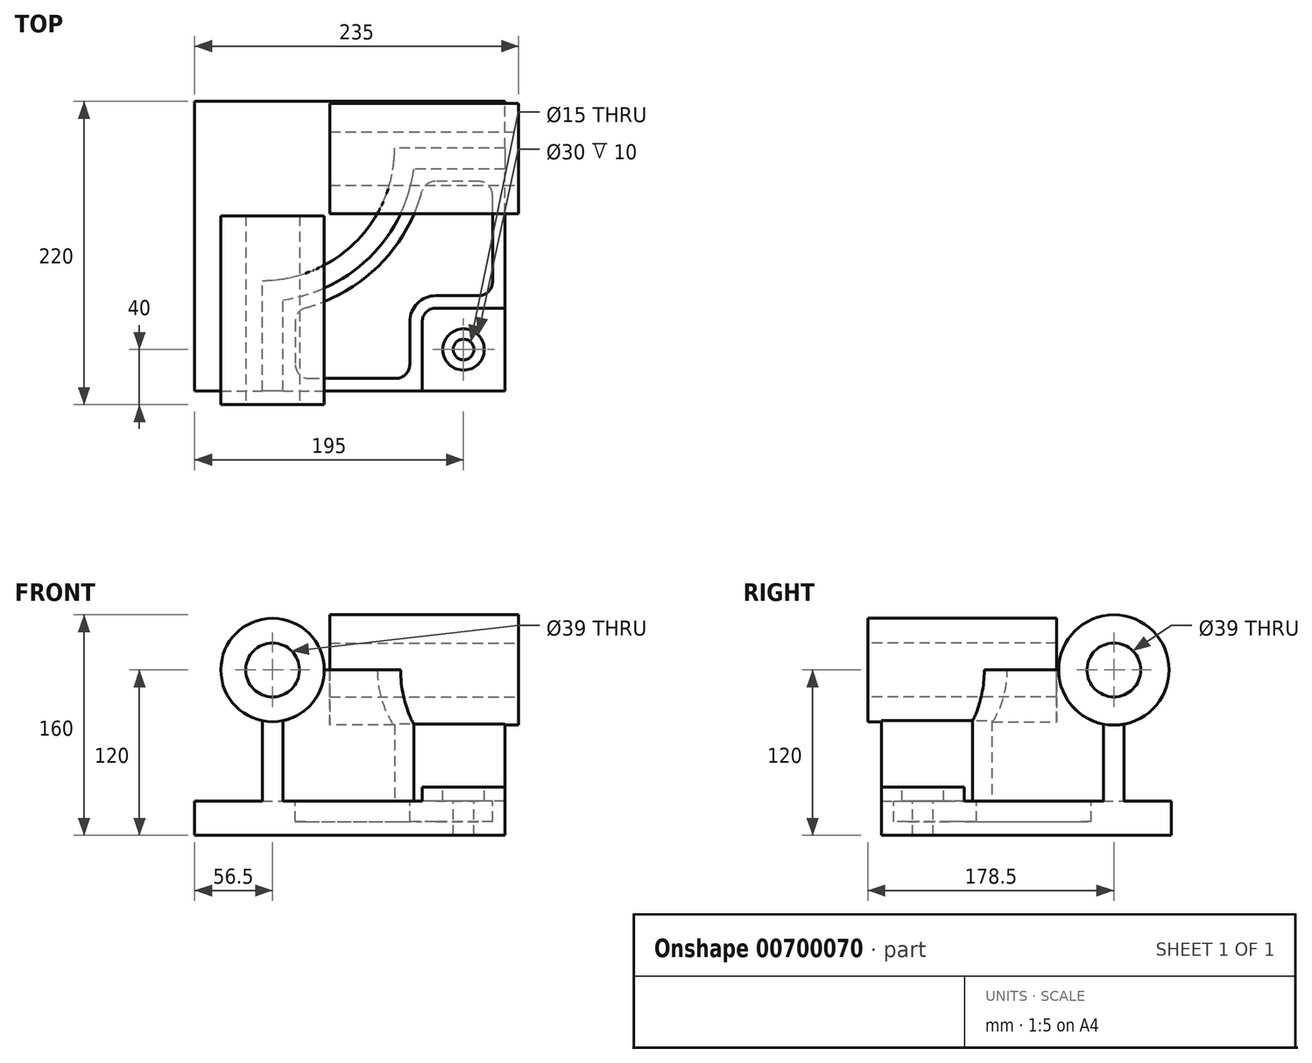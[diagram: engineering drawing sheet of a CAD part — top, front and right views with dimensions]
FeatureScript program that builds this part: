
annotation { "Feature Type Name" : "Feature", "Feature Type Description" : "" }
export const myFeature = defineFeature(function(context is Context, id is Id, definition is map)
    precondition{}
    {
        {
            var Q0;
            Q0=qCreatedBy(makeId("Top.planeOp"),FACE);
            var sketch = newSketch(context, id + "F0", { "sketchPlane" : qUnion([Q0])});
            skLineSegment(sketch, "E0.bottom", {"start": v(-112.5, -105) * mm, "end": v(112.5, -105) * mm});
            skLineSegment(sketch, "E0.top", {"start": v(-112.5, 105) * mm, "end": v(112.5, 105) * mm});
            skLineSegment(sketch, "E0.left", {"start": v(-112.5, -105) * mm, "end": v(-112.5, 105) * mm});
            skLineSegment(sketch, "E0.right", {"start": v(112.5, -105) * mm, "end": v(112.5, 105) * mm});
            skPoint(sketch, "E0.middle", {"position": v(0, 0) * mm});
            skSolve(sketch);
        }
        {
            var Q0;
            Q0=makeQuery(id+"F0.imprint","IMPRINT",FACE,{"disambiguationData":[TD([[makeQuery(id+"F0.imprint","IMPRINT",EDGE,{"derivedFrom":sQuery(id+"F0.wireOp",EDGE,"E0.bottom")}),1.0]])]});
            extrude(context, id + "F1", {"entities" : qUnion([Q0]), "depth" : 25 * mm, "offsetDistance" : 25 * mm});
        }
        {
            var Q0;
            Q0=makeQuery(id+"F1.opExtrude","CAP_FACE",FACE,{"disambiguationData":[OSD([sQuery(id+"F0.wireOp",EDGE,"E0.bottom"),sQuery(id+"F0.wireOp",EDGE,"E0.top"),sQuery(id+"F0.wireOp",EDGE,"E0.left"),sQuery(id+"F0.wireOp",EDGE,"E0.right")])],"isStart":false});
            var sketch = newSketch(context, id + "F2", { "sketchPlane" : qUnion([Q0])});
            skLineSegment(sketch, "E1", {"start": v(-90.07, -105) * mm, "end": v(-63.5, -105) * mm});
            skLineSegment(sketch, "E2", {"start": v(-63.5, -105) * mm, "end": v(-63.5, -25) * mm});
            skLineSegment(sketch, "E3", {"start": v(112.5, 71) * mm, "end": v(32.5, 71) * mm});
            skArc(sketch, "E4", {"start": v(-63.5, -25) * mm, "mid": v(4.38, 3.12) * mm, "end": v(32.5, 71) * mm});
            skLineSegment(sketch, "E5", {"start": v(-63.5, 71) * mm, "end": v(-63.5, -25) * mm, "construction": true});
            skLineSegment(sketch, "E6", {"start": v(-63.5, 71) * mm, "end": v(32.5, 71) * mm, "construction": true});
            skLineSegment(sketch, "E7.0", {"start": v(112.5, 56) * mm, "end": v(46.48, 56) * mm});
            skArc(sketch, "E7.1", {"start": v(-48.5, -38.98) * mm, "mid": v(14.99, -7.49) * mm, "end": v(46.48, 56) * mm});
            skLineSegment(sketch, "E7.2", {"start": v(-48.5, -105) * mm, "end": v(-48.5, -38.98) * mm});
            skLineSegment(sketch, "E8.0", {"start": v(112.5, -105) * mm, "end": v(112.5, 105) * mm});
            skLineSegment(sketch, "E9.0", {"start": v(-112.5, -105) * mm, "end": v(112.5, -105) * mm});
            skSolve(sketch);
        }
        {
            var Q0;
            {var subQ2=sQuery(id+"F2.wireOp",EDGE,"E2");Q0=makeQuery(id+"F2.imprint","IMPRINT",FACE,{"disambiguationData":[TD([[makeQuery(id+"F2.imprint","IMPRINT",EDGE,{"derivedFrom":subQ2}),-1.0]])]});}
            extrude(context, id + "F3", {"entities" : qUnion([Q0]), "operationType" : NewBodyOperationType.ADD, "depth" : 95 * mm, "offsetDistance" : 25 * mm});
        }
        {
            var Q0;
            Q0=makeQuery(id+"F3.boolean.opBoolean","MERGE",FACE,{"derivedFrom":[makeQuery(id+"F1.opExtrude","SWEPT_FACE",FACE,{"disambiguationData":[OSD([sQuery(id+"F0.wireOp",EDGE,"E0.bottom")])]}),makeQuery(id+"F3.opExtrude","SWEPT_FACE",FACE,{"disambiguationData":[OSD([sQuery(id+"F2.wireOp",EDGE,"E9.0")])]})]});
            var sketch = newSketch(context, id + "F4", { "sketchPlane" : qUnion([Q0])});
            skCircle(sketch, "E10", {"center": v(-56, 120) * mm, "radius": 37.5 * mm});
            skSolve(sketch);
        }
        {
            var Q0;
            Q0 = qSketchRegion(id + "F4", true);
            extrude(context, id + "F5", {"entities" : qUnion([Q0]), "operationType" : NewBodyOperationType.ADD, "depth" : 10 * mm, "offsetDistance" : 25 * mm, "hasSecondDirection" : true, "secondDirectionOppositeDirection" : true, "secondDirectionDepth" : 127 * mm});
        }
        {
            var Q0;
            Q0=makeQuery(id+"F3.boolean.opBoolean","MERGE",FACE,{"derivedFrom":[makeQuery(id+"F1.opExtrude","SWEPT_FACE",FACE,{"disambiguationData":[OSD([sQuery(id+"F0.wireOp",EDGE,"E0.right")])]}),makeQuery(id+"F3.opExtrude","SWEPT_FACE",FACE,{"disambiguationData":[OSD([sQuery(id+"F2.wireOp",EDGE,"E8.0")])]})]});
            var sketch = newSketch(context, id + "F6", { "sketchPlane" : qUnion([Q0])});
            skCircle(sketch, "E11", {"center": v(63.5, 120) * mm, "radius": 40 * mm});
            skSolve(sketch);
        }
        {
            var Q0;
            Q0 = qSketchRegion(id + "F6", true);
            extrude(context, id + "F7", {"entities" : qUnion([Q0]), "operationType" : NewBodyOperationType.ADD, "depth" : 10 * mm, "offsetDistance" : 25 * mm, "hasSecondDirection" : true, "secondDirectionOppositeDirection" : true, "secondDirectionDepth" : 127 * mm});
        }
        {
            var Q0;
            {var subQ0=sQuery(id+"F0.wireOp",EDGE,"E0.right");var subQ1=sQuery(id+"F0.wireOp",EDGE,"E0.bottom");Q0=makeQuery(id+"F3.boolean.opBoolean","SPLIT",FACE,{"disambiguationData":[TD([makeQuery(id+"F3.opExtrude","SWEPT_FACE",FACE,{"disambiguationData":[OSD([sQuery(id+"F2.wireOp",EDGE,"E7.0")])]})])],"derivedFrom":makeQuery(id+"F1.opExtrude","CAP_FACE",FACE,{"disambiguationData":[OSD([subQ1,sQuery(id+"F0.wireOp",EDGE,"E0.top"),sQuery(id+"F0.wireOp",EDGE,"E0.left"),subQ0])],"isStart":false})});}
            var sketch = newSketch(context, id + "F8", { "sketchPlane" : qUnion([Q0])});
            skLineSegment(sketch, "E12.bottom", {"start": v(112.5, -105) * mm, "end": v(52.5, -105) * mm});
            skLineSegment(sketch, "E12.top", {"start": v(112.5, -45) * mm, "end": v(52.5, -45) * mm});
            skLineSegment(sketch, "E12.left", {"start": v(112.5, -105) * mm, "end": v(112.5, -45) * mm});
            skLineSegment(sketch, "E12.right", {"start": v(52.5, -105) * mm, "end": v(52.5, -45) * mm});
            skSolve(sketch);
        }
        {
            var Q0;
            Q0 = qSketchRegion(id + "F8", true);
            extrude(context, id + "F9", {"entities" : qUnion([Q0]), "operationType" : NewBodyOperationType.ADD, "depth" : 10 * mm, "offsetDistance" : 25 * mm});
        }
        {
            var Q0;
            Q0=makeQuery(id+"F9.opExtrude","SWEPT_EDGE",EDGE,{"disambiguationData":[OSD([sQuery(id+"F8.wireOp",EDGE,"E12.top"),sQuery(id+"F8.wireOp",EDGE,"E12.right")])]});
            fillet(context, id + "F10", {"entities" : qUnion([Q0]), "radius" : 10 * mm, "tangentPropagation" : true, "allowEdgeOverflow" : false});
        }
        {
            var Q0;
            {var subQ0=sQuery(id+"F0.wireOp",EDGE,"E0.right");var subQ1=sQuery(id+"F0.wireOp",EDGE,"E0.bottom");Q0=makeQuery(id+"F3.boolean.opBoolean","SPLIT",FACE,{"disambiguationData":[TD([makeQuery(id+"F3.opExtrude","SWEPT_FACE",FACE,{"disambiguationData":[OSD([sQuery(id+"F2.wireOp",EDGE,"E7.0")])]})])],"derivedFrom":makeQuery(id+"F1.opExtrude","CAP_FACE",FACE,{"disambiguationData":[OSD([subQ1,sQuery(id+"F0.wireOp",EDGE,"E0.top"),sQuery(id+"F0.wireOp",EDGE,"E0.left"),subQ0])],"isStart":false})});}
            var sketch = newSketch(context, id + "F11", { "sketchPlane" : qUnion([Q0])});
            skLineSegment(sketch, "E13.0", {"start": v(-39.5, -46.58) * mm, "end": v(-39.5, -96) * mm});
            skArc(sketch, "E13.1", {"start": v(54.08, 47) * mm, "mid": v(21.35, -13.85) * mm, "end": v(-39.5, -46.58) * mm});
            skLineSegment(sketch, "E13.2", {"start": v(-39.5, -96) * mm, "end": v(43.5, -96) * mm});
            skLineSegment(sketch, "E13.3", {"start": v(103.5, 47) * mm, "end": v(54.08, 47) * mm});
            skLineSegment(sketch, "E13.4", {"start": v(43.5, -96) * mm, "end": v(43.5, -55) * mm});
            skArc(sketch, "E13.5", {"start": v(43.5, -55) * mm, "mid": v(49.06, -41.56) * mm, "end": v(62.5, -36) * mm});
            skLineSegment(sketch, "E13.6", {"start": v(62.5, -36) * mm, "end": v(103.5, -36) * mm});
            skLineSegment(sketch, "E13.7", {"start": v(103.5, -36) * mm, "end": v(103.5, 47) * mm});
            skSolve(sketch);
        }
        {
            var Q0;
            Q0=makeQuery(id+"F11.imprint","IMPRINT",FACE,{"disambiguationData":[TD([[makeQuery(id+"F11.imprint","IMPRINT",EDGE,{"derivedFrom":sQuery(id+"F11.wireOp",EDGE,"E13.0")}),1.0]])]});
            extrude(context, id + "F12", {"entities" : qUnion([Q0]), "operationType" : NewBodyOperationType.REMOVE, "oppositeDirection" : true, "depth" : 15 * mm, "offsetDistance" : 25 * mm});
        }
        {
            var Q0;
            Q0=makeQuery(id+"F9.opExtrude","CAP_FACE",FACE,{"disambiguationData":[OSD([sQuery(id+"F8.wireOp",EDGE,"E12.bottom"),sQuery(id+"F8.wireOp",EDGE,"E12.top"),sQuery(id+"F8.wireOp",EDGE,"E12.left"),sQuery(id+"F8.wireOp",EDGE,"E12.right")])],"isStart":false});
            var sketch = newSketch(context, id + "F13", { "sketchPlane" : qUnion([Q0])});
            skCircle(sketch, "E14", {"center": v(82.5, -75) * mm, "radius": 15 * mm});
            skSolve(sketch);
        }
        {
            var Q0;
            Q0=sQuery(id+"F13.wireOp",VERTEX,"E14.center");
            var Q1;
            Q1=makeQuery(id+"F1.opExtrude","SWEPT_BODY",BODY,{"disambiguationData":[OSD([sQuery(id+"F0.wireOp",EDGE,"E0.bottom"),sQuery(id+"F0.wireOp",EDGE,"E0.top"),sQuery(id+"F0.wireOp",EDGE,"E0.left"),sQuery(id+"F0.wireOp",EDGE,"E0.right")])]});
            hole(context, id + "F14", {"style" : HoleStyle.C_BORE, "endStyle" : HoleEndStyle.THROUGH, "holeDiameter" : 15 * mm, "cBoreDiameter" : 30 * mm, "cBoreDepth" : 10 * mm, "majorDiameter" : 5 * mm, "isTappedThrough" : true, "tappedDepth" : 12 * mm, "tapClearance" : 3, "locations" : qUnion([Q0]), "scope" : qUnion([Q1])});
        }
        {
            var Q0;
            Q0=makeQuery(id+"F12.boolean.opBoolean","COPY",EDGE,{"derivedFrom":makeQuery(id+"F12.opExtrude","SWEPT_EDGE",EDGE,{"disambiguationData":[OSD([sQuery(id+"F11.wireOp",EDGE,"E13.6"),sQuery(id+"F11.wireOp",EDGE,"E13.7")])]})});
            var Q1;
            Q1=makeQuery(id+"F12.boolean.opBoolean","COPY",EDGE,{"derivedFrom":makeQuery(id+"F12.opExtrude","SWEPT_EDGE",EDGE,{"disambiguationData":[OSD([sQuery(id+"F11.wireOp",EDGE,"E13.2"),sQuery(id+"F11.wireOp",EDGE,"E13.4")])]})});
            var Q2;
            Q2=makeQuery(id+"F12.boolean.opBoolean","COPY",EDGE,{"derivedFrom":makeQuery(id+"F12.opExtrude","SWEPT_EDGE",EDGE,{"disambiguationData":[OSD([sQuery(id+"F11.wireOp",EDGE,"E13.0"),sQuery(id+"F11.wireOp",EDGE,"E13.1")])]})});
            var Q3;
            Q3=makeQuery(id+"F12.boolean.opBoolean","COPY",EDGE,{"derivedFrom":makeQuery(id+"F12.opExtrude","SWEPT_EDGE",EDGE,{"disambiguationData":[OSD([sQuery(id+"F11.wireOp",EDGE,"E13.1"),sQuery(id+"F11.wireOp",EDGE,"E13.3")])]})});
            var Q4;
            Q4=makeQuery(id+"F12.boolean.opBoolean","COPY",EDGE,{"derivedFrom":makeQuery(id+"F12.opExtrude","SWEPT_EDGE",EDGE,{"disambiguationData":[OSD([sQuery(id+"F11.wireOp",EDGE,"E13.0"),sQuery(id+"F11.wireOp",EDGE,"E13.2")])]})});
            var Q5;
            Q5=makeQuery(id+"F12.boolean.opBoolean","COPY",EDGE,{"derivedFrom":makeQuery(id+"F12.opExtrude","SWEPT_EDGE",EDGE,{"disambiguationData":[OSD([sQuery(id+"F11.wireOp",EDGE,"E13.3"),sQuery(id+"F11.wireOp",EDGE,"E13.7")])]})});
            fillet(context, id + "F15", {"entities" : qUnion([Q0, Q1, Q2, Q3, Q4, Q5]), "radius" : 10 * mm, "tangentPropagation" : true, "allowEdgeOverflow" : false});
        }
        {
            var Q0;
            Q0=makeQuery(id+"F5.opExtrude","CAP_FACE",FACE,{"disambiguationData":[OSD([sQuery(id+"F4.wireOp",EDGE,"E10")])],"isStart":false});
            var sketch = newSketch(context, id + "F16", { "sketchPlane" : qUnion([Q0])});
            skCircle(sketch, "E15", {"center": v(-56, 120) * mm, "radius": 19.5 * mm});
            skSolve(sketch);
        }
        {
            var Q0;
            Q0 = qSketchRegion(id + "F16", true);
            extrude(context, id + "F17", {"entities" : qUnion([Q0]), "operationType" : NewBodyOperationType.REMOVE, "endBound" : BoundingType.THROUGH_ALL, "oppositeDirection" : true, "depth" : 25 * mm, "offsetDistance" : 25 * mm});
        }
        {
            var Q0;
            Q0=makeQuery(id+"F7.opExtrude","CAP_FACE",FACE,{"disambiguationData":[OSD([sQuery(id+"F6.wireOp",EDGE,"E11")])],"isStart":false});
            var sketch = newSketch(context, id + "F18", { "sketchPlane" : qUnion([Q0])});
            skCircle(sketch, "E16", {"center": v(63.5, 120) * mm, "radius": 19.5 * mm});
            skSolve(sketch);
        }
        {
            var Q0;
            Q0 = qSketchRegion(id + "F18", true);
            extrude(context, id + "F19", {"entities" : qUnion([Q0]), "operationType" : NewBodyOperationType.REMOVE, "endBound" : BoundingType.THROUGH_ALL, "oppositeDirection" : true, "depth" : 25 * mm, "offsetDistance" : 25 * mm});
        }
    });
